# Revit family: 6L-P-D
name_source: partatom
category: Lighting Fixtures
revit_build: Autodesk Revit Architecture 2012 (Build: 20110309_2315(x64)
units: mm (PartAtom-declared; Revit-internal decimal feet)

## types (6) — shared parameters
Apparent Load = 25 VA
Connector Description = Lighting Connector
Default Elevation = 48"
Description = The MOD™x family is an affordably-priced, full-featured offering with best-in-class attention to detail.
Fixture Length = MOD 6 : 4'
Frequency = 60 Hz
Is 120V = Yes
Is 277V = No
Lamp = 1000 lumens/ft
Load Classification = Lighting
Manufacturer = LITECONTROL
Manufacturer Fax = 781-293-2849
Model = 6-L-P-D
Pendent Height = 9"
Reflector Finish = Hubbell-White Glass
Voltage = 120 V
Wattage Comments = Variable Intensity technology provides specifiable lumen output/wattage
Width = 6 1/4"

## per-type parameters (varying)
| type | Product Documentation Link | Product Material | Product Page URL | URL |
| Matte White | http://cdn.columbialighting.com | Paint - Hubbell - Matte White | http://www.columbialighting.com | http://www.columbialighting.com |
| Textured Matte White | http://cdn.litecontrol.com | Paint - Hubbell - Textured Matte White | http://www.litecontrol.com | http://www.litecontrol.com |
| Light Silver | http://cdn.columbialighting.com | Paint - Hubbell - Light Silver | http://www.columbialighting.com | http://www.columbialighting.com |
| Machined Aluminum | http://cdn.columbialighting.com | Paint - Hubbell - Machined Aluminum | http://www.columbialighting.com | http://www.columbialighting.com |
| Carbon Black | http://cdn.columbialighting.com | Paint - Hubbell - Carbon Black | http://www.columbialighting.com | http://www.columbialighting.com |
| Textured Camera Black | http://cdn.columbialighting.com | Paint - Hubbell - Textured Camera Black | http://www.columbialighting.com | http://www.columbialighting.com |

## geometry (parser evidence)
native form markers: Blend x15, Sweep x2
no freeform markers — native parametric forms only
